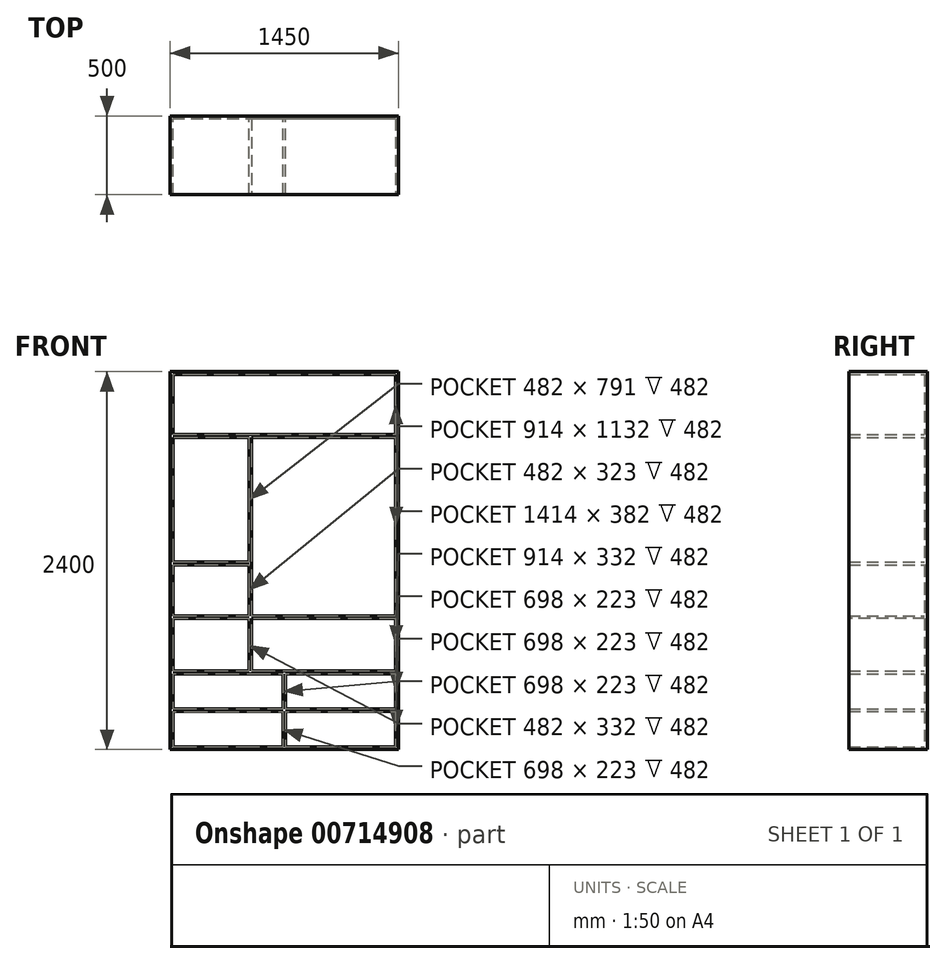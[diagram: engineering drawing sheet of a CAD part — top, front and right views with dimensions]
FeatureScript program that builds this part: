
annotation { "Feature Type Name" : "Feature", "Feature Type Description" : "" }
export const myFeature = defineFeature(function(context is Context, id is Id, definition is map)
    precondition{}
    {
        {
            var Q0;
            Q0=qCreatedBy(makeId("Front.planeOp"),FACE);
            var sketch = newSketch(context, id + "F0", { "sketchPlane" : qUnion([Q0])});
            skLineSegment(sketch, "E0.bottom", {"start": v(725, 1200) * mm, "end": v(-725, 1200) * mm});
            skLineSegment(sketch, "E0.top", {"start": v(725, -1200) * mm, "end": v(-725, -1200) * mm});
            skLineSegment(sketch, "E0.left", {"start": v(725, 1200) * mm, "end": v(725, -1200) * mm});
            skLineSegment(sketch, "E0.right", {"start": v(-725, 1200) * mm, "end": v(-725, -1200) * mm});
            skPoint(sketch, "E0.middle", {"position": v(0, 0) * mm});
            skSolve(sketch);
        }
        {
            var Q0;
            Q0=makeQuery(id+"F0.imprint","IMPRINT",FACE,{"disambiguationData":[TD([[makeQuery(id+"F0.imprint","IMPRINT",EDGE,{"derivedFrom":sQuery(id+"F0.wireOp",EDGE,"E0.bottom")}),1.0]])]});
            extrude(context, id + "F1", {"entities" : qUnion([Q0]), "depth" : 500 * mm, "offsetDistance" : 25 * mm});
        }
        {
            var Q0;
            Q0=makeQuery(id+"F1.opExtrude","CAP_FACE",FACE,{"disambiguationData":[OSD([sQuery(id+"F0.wireOp",EDGE,"E0.bottom"),sQuery(id+"F0.wireOp",EDGE,"E0.top"),sQuery(id+"F0.wireOp",EDGE,"E0.left"),sQuery(id+"F0.wireOp",EDGE,"E0.right")])],"isStart":false});
            shell(context, id + "F2", {"entities" : qUnion([Q0]), "thickness" : 18 * mm});
        }
        {
            var Q0;
            Q0=makeQuery(id+"F2.opShell","OFFSET_FACE",FACE,{"disambiguationData":[OSD([sQuery(id+"F0.wireOp",EDGE,"E0.bottom"),sQuery(id+"F0.wireOp",EDGE,"E0.top"),sQuery(id+"F0.wireOp",EDGE,"E0.left"),sQuery(id+"F0.wireOp",EDGE,"E0.right")])]});
            var sketch = newSketch(context, id + "F3", { "sketchPlane" : qUnion([Q0])});
            skLineSegment(sketch, "E1", {"start": v(-707, 800) * mm, "end": v(707, 800) * mm});
            skLineSegment(sketch, "E2", {"start": v(-707, -700) * mm, "end": v(-225, -700) * mm});
            skLineSegment(sketch, "E3.0", {"start": v(-707, 782) * mm, "end": v(-225, 782) * mm});
            skLineSegment(sketch, "E4.0", {"start": v(-707, -718) * mm, "end": v(-9, -718) * mm});
            skLineSegment(sketch, "E5", {"start": v(-707, -700) * mm, "end": v(-707, -718) * mm});
            skLineSegment(sketch, "E6", {"start": v(707, -700) * mm, "end": v(707, -718) * mm});
            skLineSegment(sketch, "E7", {"start": v(707, 800) * mm, "end": v(707, 782) * mm});
            skLineSegment(sketch, "E8", {"start": v(-707, 800) * mm, "end": v(-707, 782) * mm});
            skLineSegment(sketch, "E9.0.left", {"start": v(9, -718) * mm, "end": v(9, -941) * mm});
            skLineSegment(sketch, "E9.0.right", {"start": v(-9, -718) * mm, "end": v(-9, -941) * mm});
            skLineSegment(sketch, "E10", {"start": v(-9, -1182) * mm, "end": v(9, -1182) * mm});
            skLineSegment(sketch, "E11.trimOffspring", {"start": v(9, -718) * mm, "end": v(707, -718) * mm});
            skLineSegment(sketch, "E12.0.left", {"start": v(-707, -941) * mm, "end": v(-9, -941) * mm});
            skLineSegment(sketch, "E12.0.right", {"start": v(-707, -959) * mm, "end": v(-9, -959) * mm});
            skLineSegment(sketch, "E13", {"start": v(707, -941) * mm, "end": v(707, -959) * mm});
            skLineSegment(sketch, "E14", {"start": v(-707, -941) * mm, "end": v(-707, -959) * mm});
            skLineSegment(sketch, "E15.trimOffspring", {"start": v(9, -941) * mm, "end": v(707, -941) * mm});
            skLineSegment(sketch, "E16.trimOffspring", {"start": v(9, -959) * mm, "end": v(707, -959) * mm});
            skLineSegment(sketch, "E17.trimOffspring", {"start": v(-9, -959) * mm, "end": v(-9, -1182) * mm});
            skLineSegment(sketch, "E18.trimOffspring", {"start": v(9, -959) * mm, "end": v(9, -1182) * mm});
            skLineSegment(sketch, "E19", {"start": v(-225, 782) * mm, "end": v(-225, -700) * mm});
            skLineSegment(sketch, "E20.0", {"start": v(-207, 782) * mm, "end": v(-207, -700) * mm});
            skLineSegment(sketch, "E21.trimOffspring", {"start": v(-207, -700) * mm, "end": v(707, -700) * mm});
            skLineSegment(sketch, "E22.trimOffspring", {"start": v(-207, 782) * mm, "end": v(707, 782) * mm});
            skSolve(sketch);
        }
        {
            var Q0;
            Q0 = qSketchRegion(id + "F3", true);
            extrude(context, id + "F4", {"entities" : qUnion([Q0]), "operationType" : NewBodyOperationType.ADD, "depth" : 482 * mm, "offsetDistance" : 25 * mm});
        }
        {
            var Q0;
            {var subQ0=sQuery(id+"F0.wireOp",EDGE,"E0.right");Q0=makeQuery(id+"F4.boolean.opBoolean","SPLIT",FACE,{"disambiguationData":[TD([makeQuery(id+"F4.opExtrude","SWEPT_FACE",FACE,{"disambiguationData":[OSD([sQuery(id+"F3.wireOp",EDGE,"E2")])]})])],"derivedFrom":makeQuery(id+"F2.opShell","OFFSET_FACE",FACE,{"disambiguationData":[OSD([sQuery(id+"F0.wireOp",EDGE,"E0.bottom"),sQuery(id+"F0.wireOp",EDGE,"E0.top"),sQuery(id+"F0.wireOp",EDGE,"E0.left"),subQ0])]})});}
            var sketch = newSketch(context, id + "F5", { "sketchPlane" : qUnion([Q0])});
            skLineSegment(sketch, "E23.0.left", {"start": v(-707, -350) * mm, "end": v(707.23, -350) * mm});
            skLineSegment(sketch, "E23.0.right", {"start": v(-707, -368) * mm, "end": v(707.23, -368) * mm});
            skLineSegment(sketch, "E23.1.left", {"start": v(-707, -9) * mm, "end": v(-225, -9) * mm});
            skLineSegment(sketch, "E23.1.right", {"start": v(-707, -27) * mm, "end": v(-225, -27) * mm});
            skLineSegment(sketch, "E24", {"start": v(707.23, -350) * mm, "end": v(707.23, -368) * mm});
            skLineSegment(sketch, "E25", {"start": v(-707, -350) * mm, "end": v(-707, -368) * mm});
            skLineSegment(sketch, "E26", {"start": v(-225, -9) * mm, "end": v(-225, -27) * mm});
            skLineSegment(sketch, "E27", {"start": v(-707, -9) * mm, "end": v(-707, -27) * mm});
            skSolve(sketch);
        }
        {
            var Q0;
            Q0 = qSketchRegion(id + "F5", true);
            extrude(context, id + "F6", {"entities" : qUnion([Q0]), "operationType" : NewBodyOperationType.ADD, "depth" : 482 * mm, "offsetDistance" : 25 * mm});
        }
    });
